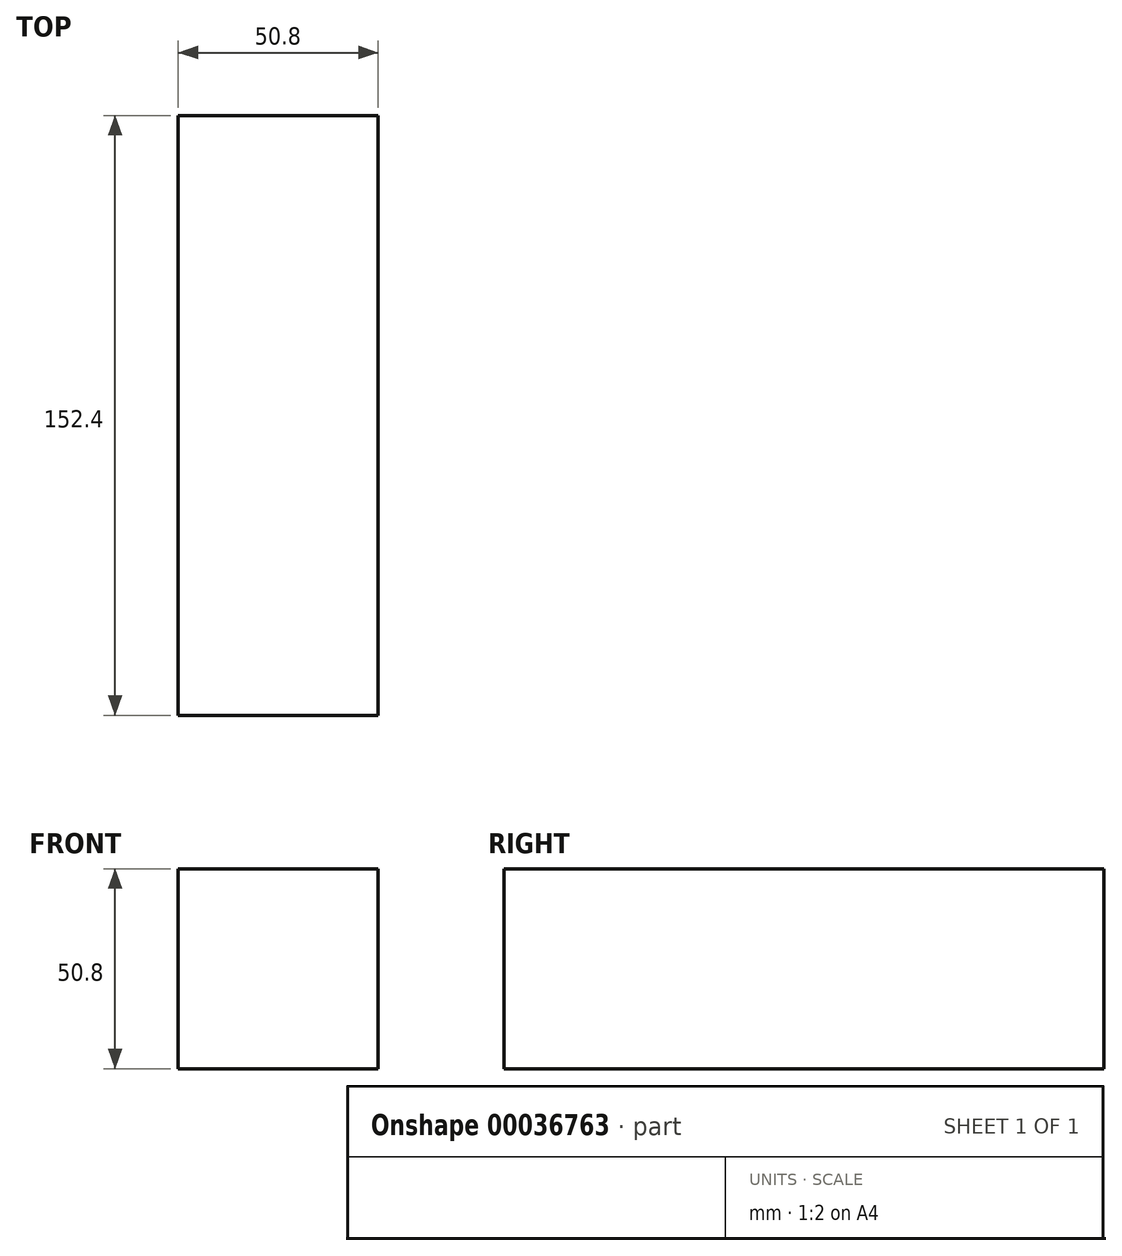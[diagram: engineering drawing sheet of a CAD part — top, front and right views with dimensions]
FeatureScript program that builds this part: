
annotation { "Feature Type Name" : "Feature", "Feature Type Description" : "" }
export const myFeature = defineFeature(function(context is Context, id is Id, definition is map)
    precondition{}
    {
        {
            var Q0;
            Q0=qCreatedBy(makeId("Front.planeOp"),FACE);
            var sketch = newSketch(context, id + "F0", { "sketchPlane" : qUnion([Q0])});
            skLineSegment(sketch, "E0.bottom", {"start": v(-20.41, 26.35) * mm, "end": v(30.39, 26.35) * mm});
            skLineSegment(sketch, "E0.top", {"start": v(-20.41, -24.45) * mm, "end": v(30.39, -24.45) * mm});
            skLineSegment(sketch, "E0.left", {"start": v(-20.41, 26.35) * mm, "end": v(-20.41, -24.45) * mm});
            skLineSegment(sketch, "E0.right", {"start": v(30.39, 26.35) * mm, "end": v(30.39, -24.45) * mm});
            skSolve(sketch);
        }
        {
            var Q0;
            Q0=makeQuery(id+"F0.imprint","IMPRINT",FACE,{"disambiguationData":[TD([[makeQuery(id+"F0.imprint","IMPRINT",EDGE,{"derivedFrom":sQuery(id+"F0.wireOp",EDGE,"E0.bottom")}),-1.0]])]});
            extrude(context, id + "F1", {"entities" : qUnion([Q0]), "depth" : 152.4 * mm});
        }
    });
